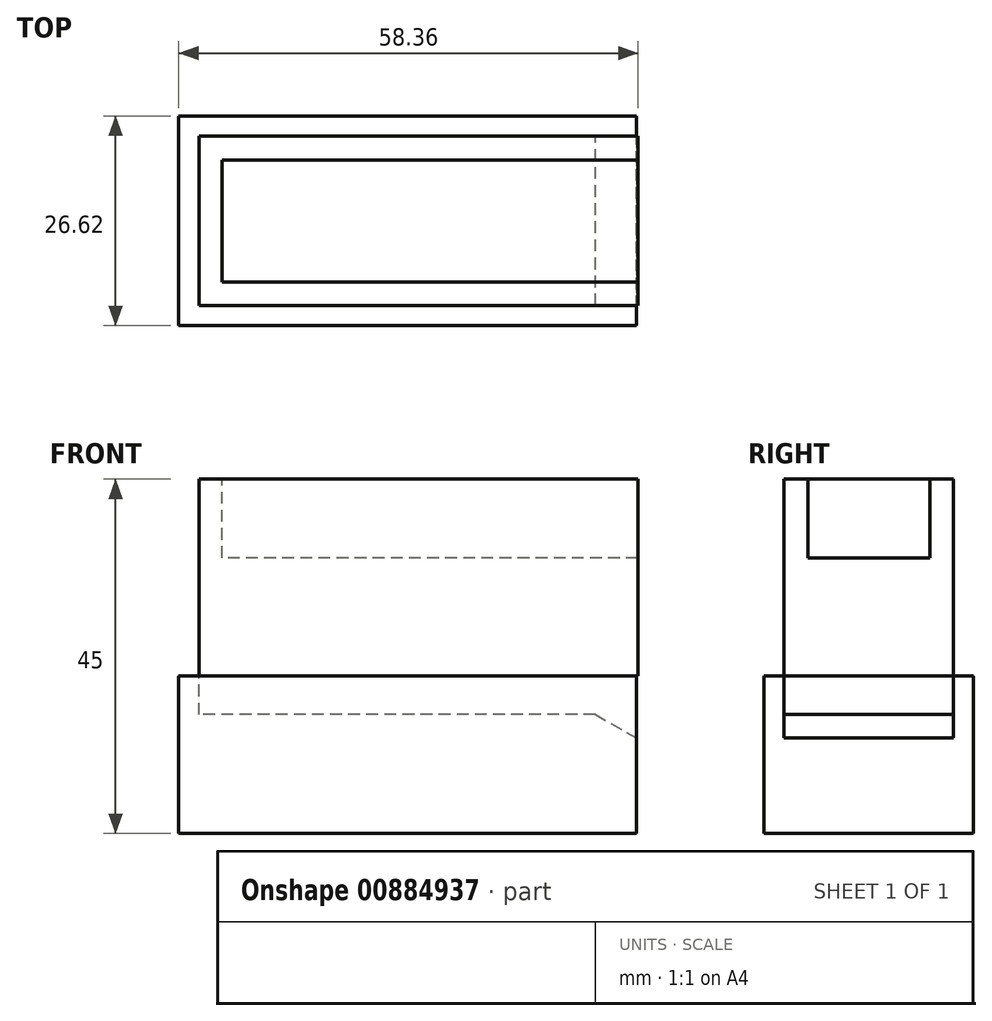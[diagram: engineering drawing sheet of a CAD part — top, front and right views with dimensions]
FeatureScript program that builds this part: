
annotation { "Feature Type Name" : "Feature", "Feature Type Description" : "" }
export const myFeature = defineFeature(function(context is Context, id is Id, definition is map)
    precondition{}
    {
        {
            var Q0;
            Q0=qCreatedBy(makeId("Top.planeOp"),FACE);
            var sketch = newSketch(context, id + "F0", { "sketchPlane" : qUnion([Q0])});
            skLineSegment(sketch, "E0.bottom", {"start": v(27.89, -10.75) * mm, "end": v(-27.89, -10.75) * mm});
            skLineSegment(sketch, "E0.top", {"start": v(27.89, 10.75) * mm, "end": v(-27.89, 10.75) * mm});
            skLineSegment(sketch, "E0.left", {"start": v(27.89, -10.75) * mm, "end": v(27.89, 10.75) * mm});
            skLineSegment(sketch, "E0.right", {"start": v(-27.89, -10.75) * mm, "end": v(-27.89, 10.75) * mm});
            skPoint(sketch, "E0.middle", {"position": v(0, 0) * mm});
            skSolve(sketch);
        }
        {
            var Q0;
            Q0=makeQuery(id+"F0.imprint","IMPRINT",FACE,{"disambiguationData":[TD([[makeQuery(id+"F0.imprint","IMPRINT",EDGE,{"derivedFrom":sQuery(id+"F0.wireOp",EDGE,"E0.bottom")}),-1.0]])]});
            extrude(context, id + "F1", {"entities" : qUnion([Q0]), "depth" : 25 * mm, "offsetDistance" : 25 * mm});
        }
        {
            var Q0;
            Q0=makeQuery(id+"F1.opExtrude","CAP_FACE",FACE,{"disambiguationData":[OSD([sQuery(id+"F0.wireOp",EDGE,"E0.bottom"),sQuery(id+"F0.wireOp",EDGE,"E0.top"),sQuery(id+"F0.wireOp",EDGE,"E0.left"),sQuery(id+"F0.wireOp",EDGE,"E0.right")])],"isStart":false});
            var sketch = newSketch(context, id + "F2", { "sketchPlane" : qUnion([Q0])});
            skLineSegment(sketch, "E1.bottom", {"start": v(27.89, 7.75) * mm, "end": v(-24.94, 7.75) * mm});
            skLineSegment(sketch, "E1.top", {"start": v(27.89, -7.75) * mm, "end": v(-24.94, -7.75) * mm});
            skLineSegment(sketch, "E1.left", {"start": v(27.89, 7.75) * mm, "end": v(27.89, -7.75) * mm});
            skLineSegment(sketch, "E1.right", {"start": v(-24.94, 7.75) * mm, "end": v(-24.94, -7.75) * mm});
            skSolve(sketch);
        }
        {
            var Q0;
            Q0=makeQuery(id+"F2.imprint","IMPRINT",FACE,{"disambiguationData":[TD([[makeQuery(id+"F2.imprint","IMPRINT",EDGE,{"derivedFrom":sQuery(id+"F2.wireOp",EDGE,"E1.bottom")}),1.0]])]});
            extrude(context, id + "F3", {"entities" : qUnion([Q0]), "operationType" : NewBodyOperationType.REMOVE, "oppositeDirection" : true, "depth" : 10 * mm, "offsetDistance" : 25 * mm});
        }
        {
            var Q0;
            Q0=qCreatedBy(makeId("Top.planeOp"),FACE);
            var sketch = newSketch(context, id + "F4", { "sketchPlane" : qUnion([Q0])});
            skLineSegment(sketch, "E2.bottom", {"start": v(27.66, -13.3) * mm, "end": v(-30.47, -13.3) * mm});
            skLineSegment(sketch, "E2.top", {"start": v(27.66, 13.3) * mm, "end": v(-30.47, 13.3) * mm});
            skLineSegment(sketch, "E2.left", {"start": v(27.66, -13.3) * mm, "end": v(27.66, 13.3) * mm});
            skLineSegment(sketch, "E2.right", {"start": v(-30.47, -13.3) * mm, "end": v(-30.47, 13.3) * mm});
            skSolve(sketch);
        }
        {
            var Q0;
            Q0=makeQuery(id+"F4.imprint","IMPRINT",FACE,{"disambiguationData":[TD([[makeQuery(id+"F4.imprint","IMPRINT",EDGE,{"derivedFrom":sQuery(id+"F4.wireOp",EDGE,"E2.bottom")}),-1.0]])]});
            extrude(context, id + "F5", {"entities" : qUnion([Q0]), "oppositeDirection" : true, "depth" : 15 * mm, "offsetDistance" : 25 * mm});
        }
        {
            var Q0;
            Q0=makeQuery(id+"F1.opExtrude","CAP_FACE",FACE,{"disambiguationData":[OSD([sQuery(id+"F0.wireOp",EDGE,"E0.bottom"),sQuery(id+"F0.wireOp",EDGE,"E0.top"),sQuery(id+"F0.wireOp",EDGE,"E0.left"),sQuery(id+"F0.wireOp",EDGE,"E0.right")])],"isStart":true});
            extrude(context, id + "F6", {"entities" : qUnion([Q0]), "operationType" : NewBodyOperationType.REMOVE, "depth" : 4.9 * mm, "offsetDistance" : 25 * mm});
        }
        {
            var Q0;
            Q0=makeQuery(id+"F5.opExtrude","CAP_FACE",FACE,{"disambiguationData":[OSD([sQuery(id+"F4.wireOp",EDGE,"E2.bottom"),sQuery(id+"F4.wireOp",EDGE,"E2.top"),sQuery(id+"F4.wireOp",EDGE,"E2.left"),sQuery(id+"F4.wireOp",EDGE,"E2.right")])],"isStart":false});
            extrude(context, id + "F7", {"entities" : qUnion([Q0]), "operationType" : NewBodyOperationType.ADD, "depth" : 5 * mm, "offsetDistance" : 25 * mm});
        }
        {
            var Q0;
            Q0=makeQuery(id+"F6.boolean.opBoolean","INTERSECT",EDGE,{"derivedFrom":[makeQuery(id+"F5.opExtrude","SWEPT_FACE",FACE,{"disambiguationData":[OSD([sQuery(id+"F4.wireOp",EDGE,"E2.left")])]}),makeQuery(id+"F6.opExtrude","CAP_FACE",FACE,{"disambiguationData":[OSD([sQuery(id+"F0.wireOp",EDGE,"E0.bottom"),sQuery(id+"F0.wireOp",EDGE,"E0.top"),sQuery(id+"F0.wireOp",EDGE,"E0.left"),sQuery(id+"F0.wireOp",EDGE,"E0.right")])],"isStart":false})]});
            chamfer(context, id + "F8", {"entities" : qUnion([Q0]), "chamferType" : ChamferType.OFFSET_ANGLE, "width" : 3 * mm, "oppositeDirection" : false, "angle" : 60 * degree, "tangentPropagation" : true});
        }
    });
